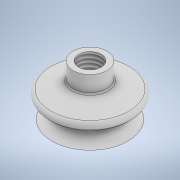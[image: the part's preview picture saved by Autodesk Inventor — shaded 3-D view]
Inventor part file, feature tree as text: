
AUTODESK INVENTOR PART (.ipt)
format: ipt  version: 2022 (Build 260153000, 153)  size: 209,920 bytes
history: native  units: mm
features: sketch x5, extrude x3, fillet x3, chamfer x2, other x1, revolve x1, hole x1
ambient origin geometry x8: Origin, YZ Plane, XZ Plane, XY Plane, X Axis, Y Axis, Z Axis, Center Point
bodies: Body1 (feature_tree)
feature tree (16):
  other  "Sólido1"
  extrude  "Extrusión1"  Depth=10.0mm TaperAngle=0.0deg
  extrude  "Extrusión2"  Depth=10.0mm TaperAngle=0.0deg
  extrude  "Extrusión3"  Depth=10.0mm TaperAngle=0.0deg
  chamfer  "Chaflán1"  Distance=15.0mm Angle=45.0deg
  chamfer  "Chaflán2"  Distance=2.5mm Angle=45.0deg
  fillet  "Empalme1"  Radius=2.5mm
  revolve  "Revolución1"  Angle=90.0deg
  fillet  "Empalme2"  Radius=2.0mm
  hole  "Agujero1"  [1 undecoded]
  fillet  "Empalme3"  [1 undecoded]
  sketch  "Boceto1"  dims[d0=45.0mm d1=10.0mm d2=0.0mm]
  sketch  "Boceto2"  dims[d3=50.0mm d4=10.0mm d5=0.0mm]
  sketch  "Boceto3"  dims[d6=20.0mm d7=10.0mm d8=0.0mm d9=15.0mm d10=5.0mm d11=45.0deg d12=2.5mm d13=7.75mm d14=45.0deg d15=2.5mm]
  sketch  "Boceto5"  dims[d16=5.0mm d17=90.0deg d18=2.0mm]
  sketch  "Boceto6"  dims[d19=13.3858mm d20=10.0mm d21=4.0mm d22=2.0mm d23=90.0deg d24=8.0mm d25=20.594885mm d26=1.0mm]
note: 2 required parameter values undecoded (feature->parameter linkage not recoverable at this tier; creation-order binding heuristic only, values carry confidence <= 0.55)
